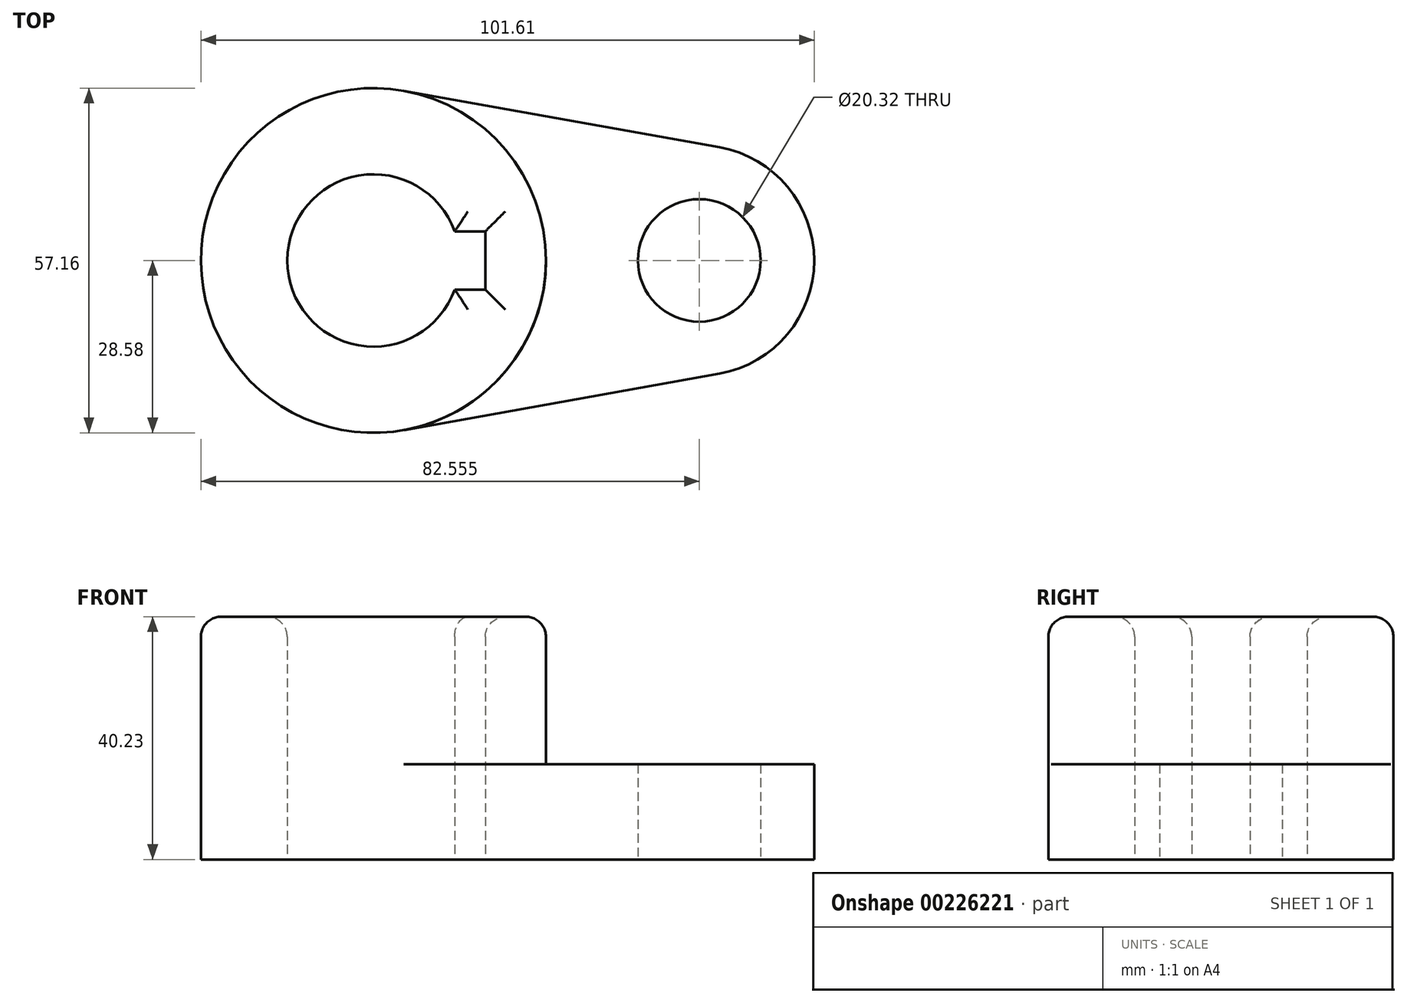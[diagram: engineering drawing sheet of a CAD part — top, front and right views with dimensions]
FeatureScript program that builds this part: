
annotation { "Feature Type Name" : "Feature", "Feature Type Description" : "" }
export const myFeature = defineFeature(function(context is Context, id is Id, definition is map)
    precondition{}
    {
        {
            var Q0;
            Q0=qCreatedBy(makeId("Top.planeOp"),FACE);
            var sketch = newSketch(context, id + "F0", { "sketchPlane" : qUnion([Q0])});
            skCircle(sketch, "E0", {"center": v(0, 0) * mm, "radius": 28.58 * mm});
            skArc(sketch, "E1", {"start": v(13.45, 4.83) * mm, "mid": v(-14.29, 0) * mm, "end": v(13.45, -4.83) * mm});
            skLineSegment(sketch, "E2.bottom", {"start": v(18.53, 4.83) * mm, "end": v(13.45, 4.83) * mm});
            skLineSegment(sketch, "E2.top", {"start": v(18.53, -4.83) * mm, "end": v(13.45, -4.83) * mm});
            skLineSegment(sketch, "E2.left", {"start": v(18.53, 4.83) * mm, "end": v(18.53, -4.83) * mm});
            skCircle(sketch, "E3", {"center": v(53.98, 0) * mm, "radius": 10.16 * mm});
            skArc(sketch, "E4", {"start": v(57.34, -18.75) * mm, "mid": v(73.03, 0) * mm, "end": v(57.34, 18.75) * mm});
            skLineSegment(sketch, "E5", {"start": v(5.04, 28.13) * mm, "end": v(57.34, 18.75) * mm});
            skLineSegment(sketch, "E6", {"start": v(5.04, -28.13) * mm, "end": v(57.34, -18.75) * mm});
            skSolve(sketch);
        }
        {
            var Q0;
            Q0=makeQuery(id+"F0.imprint","IMPRINT",FACE,{"disambiguationData":[TD([[makeQuery(id+"F0.imprint","IMPRINT",EDGE,{"derivedFrom":sQuery(id+"F0.wireOp",EDGE,"E1")}),-1.0]])]});
            extrude(context, id + "F1", {"entities" : qUnion([Q0]), "depth" : 40.23 * mm});
        }
        {
            var Q0;
            Q0 = qSketchRegion(id + "F0", true);
            extrude(context, id + "F2", {"entities" : qUnion([Q0]), "operationType" : NewBodyOperationType.ADD, "depth" : 15.77 * mm});
        }
        {
            var Q0;
            Q0=makeQuery(id+"F1.opExtrude","CAP_FACE",FACE,{"disambiguationData":[OSD([sQuery(id+"F0.wireOp",EDGE,"E0"),sQuery(id+"F0.wireOp",EDGE,"E1"),sQuery(id+"F0.wireOp",EDGE,"E2.bottom"),sQuery(id+"F0.wireOp",EDGE,"E2.top"),sQuery(id+"F0.wireOp",EDGE,"E2.left"),sQuery(id+"F0.wireOp",EDGE,"E5"),sQuery(id+"F0.wireOp",EDGE,"E6")])],"isStart":false});
            fillet(context, id + "F3", {"entities" : qUnion([Q0]), "radius" : 3.3 * mm, "tangentPropagation" : true, "allowEdgeOverflow" : false});
        }
    });
